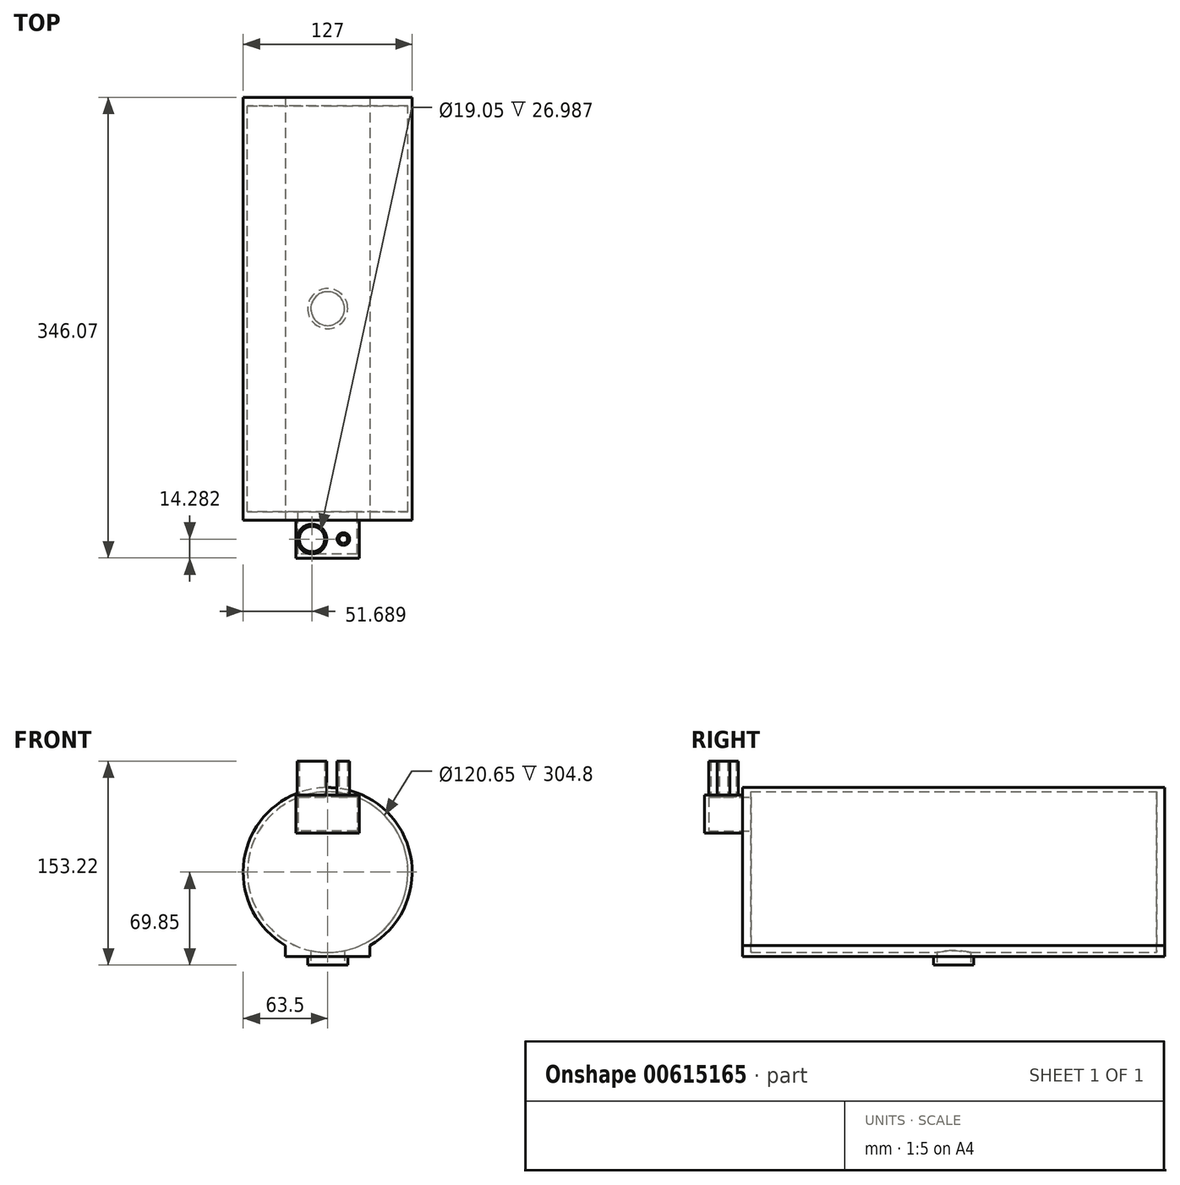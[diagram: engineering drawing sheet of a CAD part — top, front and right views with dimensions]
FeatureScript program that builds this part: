
annotation { "Feature Type Name" : "Feature", "Feature Type Description" : "" }
export const myFeature = defineFeature(function(context is Context, id is Id, definition is map)
    precondition{}
    {
        {
            var Q0;
            Q0=qCreatedBy(makeId("Front.planeOp"),FACE);
            var sketch = newSketch(context, id + "F0", { "sketchPlane" : qUnion([Q0])});
            skCircle(sketch, "E0", {"center": v(0, 0) * mm, "radius": 63.5 * mm});
            skCircle(sketch, "E1", {"center": v(0, 0) * mm, "radius": 60.33 * mm});
            skSolve(sketch);
        }
        {
            var Q0;
            Q0 = qSketchRegion(id + "F0", true);
            extrude(context, id + "F1", {"entities" : qUnion([Q0]), "depth" : 304.8 * mm, "offsetDistance" : 25.4 * mm, "symmetric" : true});
        }
        {
            var Q0;
            Q0=makeQuery(id+"F1.opExtrude","CAP_FACE",FACE,{"disambiguationData":[OSD([sQuery(id+"F0.wireOp",EDGE,"E0"),sQuery(id+"F0.wireOp",EDGE,"E1")])],"isStart":false});
            var sketch = newSketch(context, id + "F2", { "sketchPlane" : qUnion([Q0])});
            skCircle(sketch, "E2", {"center": v(0, 0) * mm, "radius": 63.5 * mm});
            skSolve(sketch);
        }
        {
            var Q0;
            Q0 = qSketchRegion(id + "F2", true);
            extrude(context, id + "F3", {"entities" : qUnion([Q0]), "operationType" : NewBodyOperationType.ADD, "depth" : 6.35 * mm, "offsetDistance" : 25.4 * mm});
        }
        {
            var Q0;
            Q0=makeQuery(id+"F1.opExtrude","CAP_FACE",FACE,{"disambiguationData":[OSD([sQuery(id+"F0.wireOp",EDGE,"E0"),sQuery(id+"F0.wireOp",EDGE,"E1")])],"isStart":true});
            var sketch = newSketch(context, id + "F4", { "sketchPlane" : qUnion([Q0])});
            skCircle(sketch, "E3", {"center": v(0, 0) * mm, "radius": 63.5 * mm});
            skSolve(sketch);
        }
        {
            var Q0;
            Q0 = qSketchRegion(id + "F4", true);
            extrude(context, id + "F5", {"entities" : qUnion([Q0]), "operationType" : NewBodyOperationType.ADD, "depth" : 6.35 * mm, "offsetDistance" : 25.4 * mm});
        }
        {
            var Q0;
            Q0=makeQuery(id+"F3.opExtrude","CAP_FACE",FACE,{"disambiguationData":[OSD([sQuery(id+"F2.wireOp",EDGE,"E2")])],"isStart":false});
            var sketch = newSketch(context, id + "F6", { "sketchPlane" : qUnion([Q0])});
            skPoint(sketch, "E4.middle", {"position": v(0, 0) * mm});
            skLineSegment(sketch, "E5", {"start": v(-31.75, -63.5) * mm, "end": v(-31.75, -55) * mm});
            skLineSegment(sketch, "E6", {"start": v(-31.75, -55) * mm, "end": v(0, -63.5) * mm});
            skLineSegment(sketch, "E7", {"start": v(0, -63.5) * mm, "end": v(31.75, -55) * mm});
            skLineSegment(sketch, "E8", {"start": v(31.75, -55) * mm, "end": v(31.75, -63.5) * mm});
            skLineSegment(sketch, "E9", {"start": v(-31.75, -63.5) * mm, "end": v(31.75, -63.5) * mm});
            skSolve(sketch);
        }
        {
            var Q0;
            Q0 = qSketchRegion(id + "F6", true);
            extrude(context, id + "F7", {"entities" : qUnion([Q0]), "operationType" : NewBodyOperationType.ADD, "oppositeDirection" : true, "depth" : 317.5 * mm, "offsetDistance" : 25.4 * mm});
        }
        {
            var Q0;
            {var subQ0=sQuery(id+"F6.wireOp",EDGE,"E9");Q0=makeQuery(id+"F7.boolean.opBoolean","MERGE",FACE,{"derivedFrom":[makeQuery(id+"F7.opExtrude","SWEPT_FACE",FACE,{"disambiguationData":[OSD([subQ0]),TDD([makeQuery(id+"F6.imprint","IMPRINT",EDGE,{"disambiguationData":[TD([[makeQuery(id+"F6.imprint","INTERSECT",VERTEX,{"derivedFrom":[sQuery(id+"F6.wireOp",EDGE,"E5"),subQ0]}),-1.0]])],"derivedFrom":subQ0})])]}),makeQuery(id+"F7.opExtrude","SWEPT_FACE",FACE,{"disambiguationData":[OSD([subQ0]),TDD([makeQuery(id+"F6.imprint","IMPRINT",EDGE,{"disambiguationData":[TD([[makeQuery(id+"F6.imprint","INTERSECT",VERTEX,{"derivedFrom":[sQuery(id+"F6.wireOp",EDGE,"E8"),subQ0]}),1.0]])],"derivedFrom":subQ0})])]})]});}
            var sketch = newSketch(context, id + "F8", { "sketchPlane" : qUnion([Q0])});
            skCircle(sketch, "E10", {"center": v(0, 0) * mm, "radius": 12.7 * mm});
            skSolve(sketch);
        }
        {
            var Q0;
            Q0 = qSketchRegion(id + "F8", true);
            extrude(context, id + "F9", {"entities" : qUnion([Q0]), "operationType" : NewBodyOperationType.REMOVE, "oppositeDirection" : true, "depth" : 25.4 * mm, "offsetDistance" : 25.4 * mm});
        }
        {
            var Q0;
            {var subQ0=sQuery(id+"F6.wireOp",EDGE,"E9");Q0=makeQuery(id+"F7.boolean.opBoolean","MERGE",FACE,{"derivedFrom":[makeQuery(id+"F7.opExtrude","SWEPT_FACE",FACE,{"disambiguationData":[OSD([subQ0]),TDD([makeQuery(id+"F6.imprint","IMPRINT",EDGE,{"disambiguationData":[TD([[makeQuery(id+"F6.imprint","INTERSECT",VERTEX,{"derivedFrom":[sQuery(id+"F6.wireOp",EDGE,"E5"),subQ0]}),-1.0]])],"derivedFrom":subQ0})])]}),makeQuery(id+"F7.opExtrude","SWEPT_FACE",FACE,{"disambiguationData":[OSD([subQ0]),TDD([makeQuery(id+"F6.imprint","IMPRINT",EDGE,{"disambiguationData":[TD([[makeQuery(id+"F6.imprint","INTERSECT",VERTEX,{"derivedFrom":[sQuery(id+"F6.wireOp",EDGE,"E8"),subQ0]}),1.0]])],"derivedFrom":subQ0})])]})]});}
            var sketch = newSketch(context, id + "F10", { "sketchPlane" : qUnion([Q0])});
            skCircle(sketch, "E11", {"center": v(0, 0) * mm, "radius": 12.7 * mm});
            skCircle(sketch, "E12", {"center": v(0, 0) * mm, "radius": 15.07 * mm});
            skSolve(sketch);
        }
        {
            var Q0;
            Q0 = qSketchRegion(id + "F10", true);
            extrude(context, id + "F11", {"entities" : qUnion([Q0]), "operationType" : NewBodyOperationType.ADD, "depth" : 6.35 * mm, "offsetDistance" : 25.4 * mm});
        }
        {
            var Q0;
            {var subQ0=sQuery(id+"F6.wireOp",EDGE,"E9");Q0=makeQuery(id+"F7.boolean.opBoolean","MERGE",FACE,{"derivedFrom":[makeQuery(id+"F3.opExtrude","CAP_FACE",FACE,{"disambiguationData":[OSD([sQuery(id+"F2.wireOp",EDGE,"E2")])],"isStart":false}),makeQuery(id+"F7.opExtrude","CAP_FACE",FACE,{"disambiguationData":[OSD([sQuery(id+"F6.wireOp",EDGE,"E5"),sQuery(id+"F6.wireOp",EDGE,"E6"),subQ0])],"isStart":true}),makeQuery(id+"F7.opExtrude","CAP_FACE",FACE,{"disambiguationData":[OSD([sQuery(id+"F6.wireOp",EDGE,"E7"),sQuery(id+"F6.wireOp",EDGE,"E8"),subQ0])],"isStart":true})]});}
            var sketch = newSketch(context, id + "F12", { "sketchPlane" : qUnion([Q0])});
            skLineSegment(sketch, "E13", {"start": v(0, 0) * mm, "end": v(-0.17, 43.68) * mm});
            skLineSegment(sketch, "E14.bottom", {"start": v(22.05, 56.38) * mm, "end": v(-22.4, 56.38) * mm});
            skLineSegment(sketch, "E14.top", {"start": v(22.05, 30.98) * mm, "end": v(-22.4, 30.98) * mm});
            skLineSegment(sketch, "E14.left", {"start": v(22.05, 56.38) * mm, "end": v(22.05, 30.98) * mm});
            skLineSegment(sketch, "E14.right", {"start": v(-22.4, 56.38) * mm, "end": v(-22.4, 30.98) * mm});
            skPoint(sketch, "E14.middle", {"position": v(-0.17, 43.68) * mm});
            skLineSegment(sketch, "E15.bottom", {"start": v(23.64, 57.97) * mm, "end": v(-23.98, 57.97) * mm});
            skLineSegment(sketch, "E15.top", {"start": v(23.64, 29.4) * mm, "end": v(-23.98, 29.4) * mm});
            skLineSegment(sketch, "E15.left", {"start": v(23.64, 57.97) * mm, "end": v(23.64, 29.4) * mm});
            skLineSegment(sketch, "E15.right", {"start": v(-23.98, 57.97) * mm, "end": v(-23.98, 29.4) * mm});
            skSolve(sketch);
        }
        {
            var Q0;
            Q0 = qSketchRegion(id + "F12", true);
            extrude(context, id + "F13", {"entities" : qUnion([Q0]), "operationType" : NewBodyOperationType.ADD, "depth" : 25.4 * mm, "offsetDistance" : 25.4 * mm});
        }
        {
            var Q0;
            {var subQ0=sQuery(id+"F6.wireOp",EDGE,"E9");Q0=makeQuery(id+"F13.boolean.opBoolean","SPLIT",FACE,{"disambiguationData":[TD([makeQuery(id+"F13.opExtrude","SWEPT_FACE",FACE,{"disambiguationData":[OSD([sQuery(id+"F12.wireOp",EDGE,"E14.bottom")])]})])],"derivedFrom":makeQuery(id+"F7.boolean.opBoolean","MERGE",FACE,{"derivedFrom":[makeQuery(id+"F3.opExtrude","CAP_FACE",FACE,{"disambiguationData":[OSD([sQuery(id+"F2.wireOp",EDGE,"E2")])],"isStart":false}),makeQuery(id+"F7.opExtrude","CAP_FACE",FACE,{"disambiguationData":[OSD([sQuery(id+"F6.wireOp",EDGE,"E5"),sQuery(id+"F6.wireOp",EDGE,"E6"),subQ0])],"isStart":true}),makeQuery(id+"F7.opExtrude","CAP_FACE",FACE,{"disambiguationData":[OSD([sQuery(id+"F6.wireOp",EDGE,"E7"),sQuery(id+"F6.wireOp",EDGE,"E8"),subQ0])],"isStart":true})]})});}
            var sketch = newSketch(context, id + "F14", { "sketchPlane" : qUnion([Q0])});
            skLineSegment(sketch, "E16", {"start": v(-0.17, 30.98) * mm, "end": v(-0.17, 43.68) * mm});
            skLineSegment(sketch, "E17.bottom", {"start": v(22.05, 56.38) * mm, "end": v(-22.4, 56.38) * mm});
            skLineSegment(sketch, "E17.top", {"start": v(22.05, 30.98) * mm, "end": v(-22.4, 30.98) * mm});
            skLineSegment(sketch, "E17.left", {"start": v(22.05, 56.38) * mm, "end": v(22.05, 30.98) * mm});
            skLineSegment(sketch, "E17.right", {"start": v(-22.4, 56.38) * mm, "end": v(-22.4, 30.98) * mm});
            skPoint(sketch, "E17.middle", {"position": v(-0.17, 43.68) * mm});
            skSolve(sketch);
        }
        {
            var Q0;
            Q0 = qSketchRegion(id + "F14", true);
            extrude(context, id + "F15", {"entities" : qUnion([Q0]), "operationType" : NewBodyOperationType.REMOVE, "oppositeDirection" : true, "depth" : 6.35 * mm, "offsetDistance" : 25.4 * mm});
        }
        {
            var Q0;
            Q0=makeQuery(id+"F13.opExtrude","CAP_FACE",FACE,{"disambiguationData":[OSD([sQuery(id+"F12.wireOp",EDGE,"E14.bottom"),sQuery(id+"F12.wireOp",EDGE,"E14.top"),sQuery(id+"F12.wireOp",EDGE,"E14.left"),sQuery(id+"F12.wireOp",EDGE,"E14.right"),sQuery(id+"F12.wireOp",EDGE,"E15.bottom"),sQuery(id+"F12.wireOp",EDGE,"E15.top"),sQuery(id+"F12.wireOp",EDGE,"E15.left"),sQuery(id+"F12.wireOp",EDGE,"E15.right")])],"isStart":false});
            var sketch = newSketch(context, id + "F16", { "sketchPlane" : qUnion([Q0])});
            skLineSegment(sketch, "E18.bottom", {"start": v(-23.98, 57.97) * mm, "end": v(23.64, 57.97) * mm});
            skLineSegment(sketch, "E18.top", {"start": v(-23.98, 29.4) * mm, "end": v(23.64, 29.4) * mm});
            skLineSegment(sketch, "E18.left", {"start": v(-23.98, 57.97) * mm, "end": v(-23.98, 29.4) * mm});
            skLineSegment(sketch, "E18.right", {"start": v(23.64, 57.97) * mm, "end": v(23.64, 29.4) * mm});
            skSolve(sketch);
        }
        {
            var Q0;
            Q0 = qSketchRegion(id + "F16", true);
            extrude(context, id + "F17", {"entities" : qUnion([Q0]), "operationType" : NewBodyOperationType.ADD, "depth" : 3.17 * mm, "offsetDistance" : 25.4 * mm});
        }
        {
            var Q0;
            Q0=makeQuery(id+"F17.boolean.opBoolean","MERGE",FACE,{"derivedFrom":[makeQuery(id+"F13.opExtrude","SWEPT_FACE",FACE,{"disambiguationData":[OSD([sQuery(id+"F12.wireOp",EDGE,"E15.bottom")])]}),makeQuery(id+"F17.opExtrude","SWEPT_FACE",FACE,{"disambiguationData":[OSD([sQuery(id+"F16.wireOp",EDGE,"E18.bottom")])]})]});
            var sketch = newSketch(context, id + "F18", { "sketchPlane" : qUnion([Q0])});
            skLineSegment(sketch, "E19", {"start": v(0, -173.04) * mm, "end": v(11.82, -173.04) * mm});
            skLineSegment(sketch, "E20", {"start": v(0, -173.04) * mm, "end": v(-11.81, -173.04) * mm});
            skCircle(sketch, "E21", {"center": v(-11.81, -173.04) * mm, "radius": 9.53 * mm});
            skCircle(sketch, "E22", {"center": v(-11.81, -173.04) * mm, "radius": 11.11 * mm});
            skCircle(sketch, "E23", {"center": v(11.82, -173.04) * mm, "radius": 3.18 * mm});
            skCircle(sketch, "E24", {"center": v(11.82, -173.04) * mm, "radius": 4.76 * mm});
            skSolve(sketch);
        }
        {
            var Q0;
            Q0 = qSketchRegion(id + "F18", true);
            extrude(context, id + "F19", {"entities" : qUnion([Q0]), "operationType" : NewBodyOperationType.ADD, "depth" : 25.4 * mm, "offsetDistance" : 25.4 * mm});
        }
        {
            var Q0;
            Q0=makeQuery(id+"F19.boolean.opBoolean","SPLIT",FACE,{"disambiguationData":[TD([makeQuery(id+"F19.opExtrude","SWEPT_FACE",FACE,{"disambiguationData":[OSD([sQuery(id+"F18.wireOp",EDGE,"E21")])]})])],"derivedFrom":makeQuery(id+"F17.boolean.opBoolean","MERGE",FACE,{"derivedFrom":[makeQuery(id+"F13.opExtrude","SWEPT_FACE",FACE,{"disambiguationData":[OSD([sQuery(id+"F12.wireOp",EDGE,"E15.bottom")])]}),makeQuery(id+"F17.opExtrude","SWEPT_FACE",FACE,{"disambiguationData":[OSD([sQuery(id+"F16.wireOp",EDGE,"E18.bottom")])]})]})});
            var sketch = newSketch(context, id + "F20", { "sketchPlane" : qUnion([Q0])});
            skCircle(sketch, "E25", {"center": v(-11.81, -173.04) * mm, "radius": 9.53 * mm});
            skLineSegment(sketch, "E26", {"start": v(-11.81, -173.04) * mm, "end": v(11.81, -173.04) * mm});
            skCircle(sketch, "E27", {"center": v(11.81, -173.04) * mm, "radius": 3.18 * mm});
            skSolve(sketch);
        }
        {
            var Q0;
            Q0 = qSketchRegion(id + "F20", true);
            extrude(context, id + "F21", {"entities" : qUnion([Q0]), "operationType" : NewBodyOperationType.REMOVE, "oppositeDirection" : true, "depth" : 25.4 * mm, "offsetDistance" : 25.4 * mm});
        }
        {
            var Q0;
            Q0 = qSketchRegion(id + "F20", true);
            extrude(context, id + "F22", {"entities" : qUnion([Q0]), "operationType" : NewBodyOperationType.REMOVE, "oppositeDirection" : true, "depth" : 25.4 * mm, "offsetDistance" : 25.4 * mm});
        }
    });
